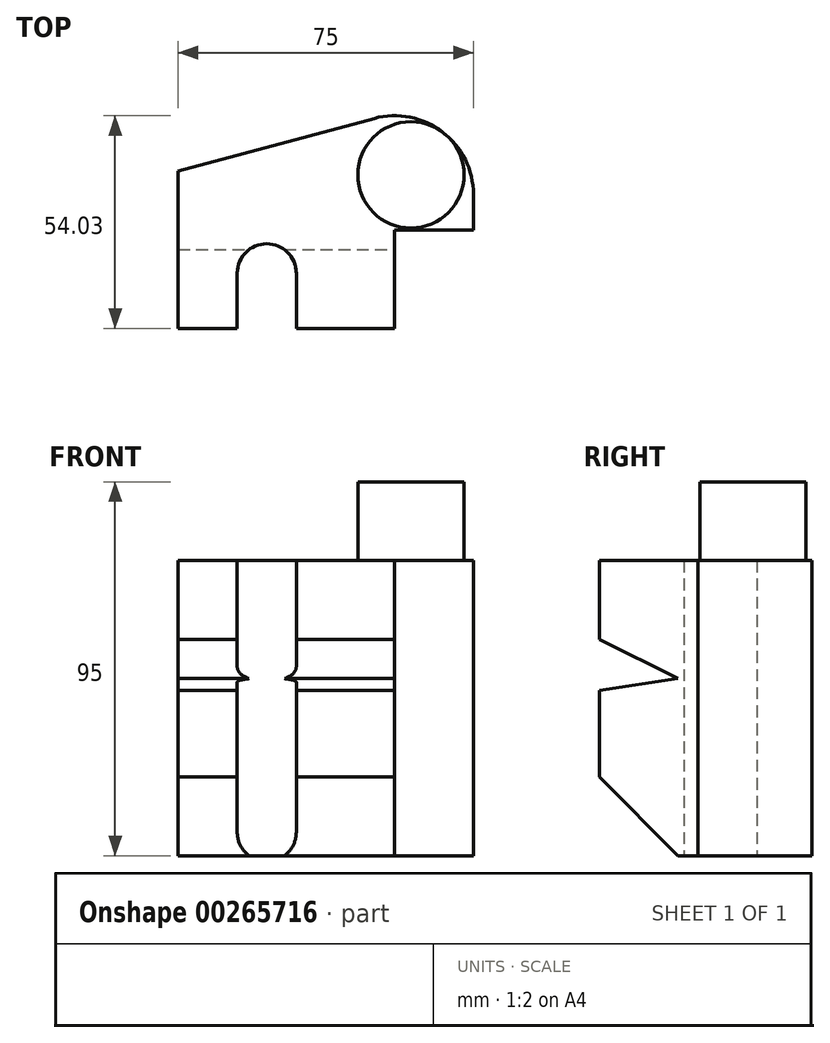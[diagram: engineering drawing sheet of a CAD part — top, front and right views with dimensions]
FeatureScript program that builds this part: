
annotation { "Feature Type Name" : "Feature", "Feature Type Description" : "" }
export const myFeature = defineFeature(function(context is Context, id is Id, definition is map)
    precondition{}
    {
        {
            var Q0;
            Q0=qCreatedBy(makeId("Top.planeOp"),FACE);
            var sketch = newSketch(context, id + "F0", { "sketchPlane" : qUnion([Q0])});
            skLineSegment(sketch, "E0", {"start": v(0, 0) * mm, "end": v(15, 0) * mm});
            skLineSegment(sketch, "E1", {"start": v(15, 0) * mm, "end": v(15, 14) * mm});
            skLineSegment(sketch, "E2", {"start": v(30, 14) * mm, "end": v(30, 0) * mm});
            skLineSegment(sketch, "E3", {"start": v(30, 0) * mm, "end": v(55, 0) * mm});
            skLineSegment(sketch, "E4", {"start": v(55, 0) * mm, "end": v(55, 25) * mm});
            skLineSegment(sketch, "E5", {"start": v(55, 25) * mm, "end": v(75, 25) * mm});
            skLineSegment(sketch, "E6", {"start": v(75, 25) * mm, "end": v(75, 34.03) * mm});
            skLineSegment(sketch, "E7", {"start": v(49.82, 53.35) * mm, "end": v(0, 40) * mm});
            skLineSegment(sketch, "E8", {"start": v(0, 40) * mm, "end": v(0, 0) * mm});
            skArc(sketch, "E9", {"start": v(30, 14) * mm, "mid": v(22.5, 21.5) * mm, "end": v(15, 14) * mm});
            skPoint(sketch, "E10.visualSharp", {"position": v(75, 60.1) * mm});
            skArc(sketch, "E10.filletArc", {"start": v(75, 34.03) * mm, "mid": v(67.18, 49.9) * mm, "end": v(49.82, 53.35) * mm});
            skSolve(sketch);
        }
        {
            var Q0;
            Q0=makeQuery(id+"F0.imprint","IMPRINT",FACE,{"disambiguationData":[TD([[makeQuery(id+"F0.imprint","IMPRINT",EDGE,{"derivedFrom":sQuery(id+"F0.wireOp",EDGE,"E0")}),1.0]])]});
            extrude(context, id + "F1", {"entities" : qUnion([Q0]), "depth" : 75 * mm});
        }
        {
            var Q0;
            Q0=makeQuery(id+"F1.opExtrude","SWEPT_FACE",FACE,{"disambiguationData":[OSD([sQuery(id+"F0.wireOp",EDGE,"E4")])]});
            var sketch = newSketch(context, id + "F2", { "sketchPlane" : qUnion([Q0])});
            skPoint(sketch, "E11", {"position": v(0, 55) * mm});
            skPoint(sketch, "E12", {"position": v(20, 45) * mm});
            skLineSegment(sketch, "E13", {"start": v(0, 55) * mm, "end": v(20, 45) * mm});
            skLineSegment(sketch, "E14", {"start": v(20, 45) * mm, "end": v(0, 42.03) * mm});
            skLineSegment(sketch, "E15", {"start": v(0, 20) * mm, "end": v(20, 0) * mm});
            skSolve(sketch);
        }
        {
            var Q0;
            {var subQ0=sQuery(id+"F2.wireOp",EDGE,"E13");Q0=makeQuery(id+"F2.imprint","IMPRINT",FACE,{"disambiguationData":[TD([[makeQuery(id+"F2.imprint","IMPRINT",EDGE,{"derivedFrom":subQ0}),-1.0]])]});}
            var Q1;
            {var subQ0=sQuery(id+"F2.wireOp",EDGE,"E15");Q1=makeQuery(id+"F2.imprint","IMPRINT",FACE,{"disambiguationData":[TD([[makeQuery(id+"F2.imprint","IMPRINT",EDGE,{"derivedFrom":subQ0}),-1.0]])]});}
            extrude(context, id + "F3", {"entities" : qUnion([Q0, Q1]), "operationType" : NewBodyOperationType.REMOVE, "oppositeDirection" : true, "depth" : 60 * mm});
        }
        {
            var Q0;
            Q0=makeQuery(id+"F1.opExtrude","CAP_FACE",FACE,{"disambiguationData":[OSD([sQuery(id+"F0.wireOp",EDGE,"E0"),sQuery(id+"F0.wireOp",EDGE,"E1"),sQuery(id+"F0.wireOp",EDGE,"E2"),sQuery(id+"F0.wireOp",EDGE,"E3"),sQuery(id+"F0.wireOp",EDGE,"E4"),sQuery(id+"F0.wireOp",EDGE,"E5"),sQuery(id+"F0.wireOp",EDGE,"E6"),sQuery(id+"F0.wireOp",EDGE,"E7"),sQuery(id+"F0.wireOp",EDGE,"E8"),sQuery(id+"F0.wireOp",EDGE,"E9"),sQuery(id+"F0.wireOp",EDGE,"E10.filletArc")])],"isStart":false});
            var sketch = newSketch(context, id + "F4", { "sketchPlane" : qUnion([Q0])});
            skCircle(sketch, "E16", {"center": v(59.13, 39) * mm, "radius": 13.5 * mm});
            skSolve(sketch);
        }
        {
            var Q0;
            Q0=makeQuery(id+"F4.imprint","IMPRINT",FACE,{"disambiguationData":[TD([[makeQuery(id+"F4.imprint","IMPRINT",EDGE,{"derivedFrom":sQuery(id+"F4.wireOp",EDGE,"E16")}),1.0]])]});
            extrude(context, id + "F5", {"entities" : qUnion([Q0]), "operationType" : NewBodyOperationType.ADD, "depth" : 20 * mm});
        }
    });
